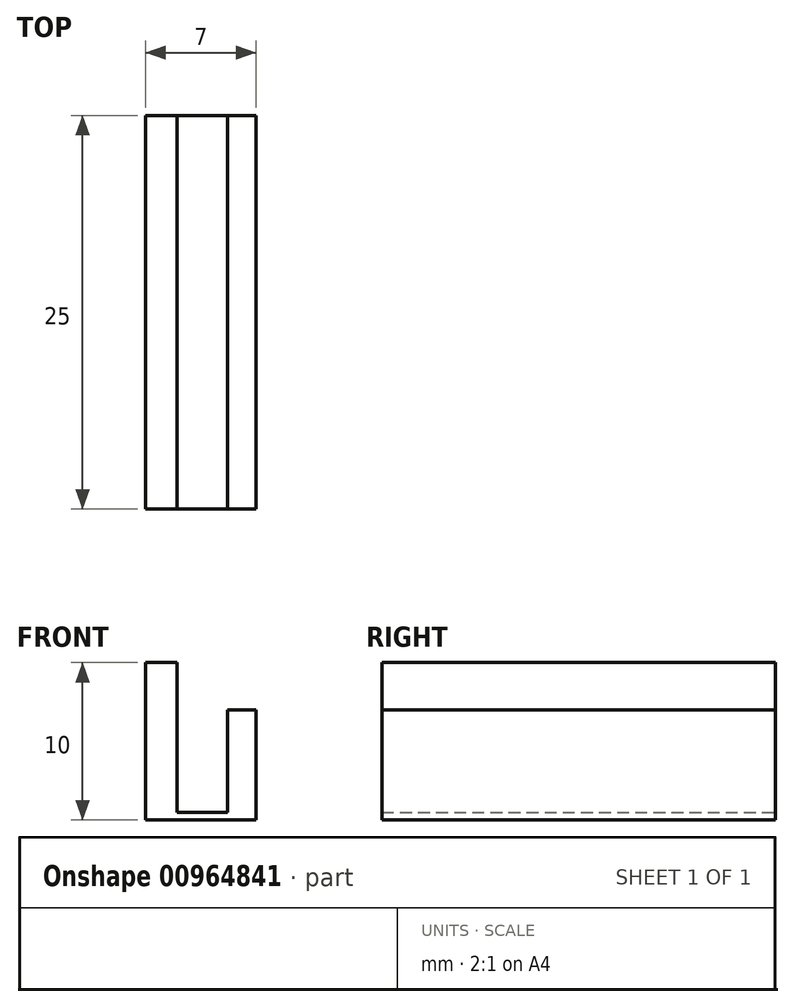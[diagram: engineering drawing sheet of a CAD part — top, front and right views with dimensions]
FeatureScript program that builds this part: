
annotation { "Feature Type Name" : "Feature", "Feature Type Description" : "" }
export const myFeature = defineFeature(function(context is Context, id is Id, definition is map)
    precondition{}
    {
        {
            var Q0;
            Q0=qCreatedBy(makeId("Front.planeOp"),FACE);
            var sketch = newSketch(context, id + "F0", { "sketchPlane" : qUnion([Q0])});
            skLineSegment(sketch, "E0", {"start": v(0, 0) * mm, "end": v(7, 0) * mm});
            skLineSegment(sketch, "E1", {"start": v(0, 0) * mm, "end": v(0, 2) * mm});
            skLineSegment(sketch, "E2", {"start": v(0, 2) * mm, "end": v(0, 10) * mm});
            skLineSegment(sketch, "E3", {"start": v(0, 10) * mm, "end": v(2, 10) * mm});
            skLineSegment(sketch, "E4", {"start": v(2, 10) * mm, "end": v(2, 0.5) * mm});
            skLineSegment(sketch, "E5", {"start": v(2, 0.5) * mm, "end": v(5.2, 0.5) * mm});
            skLineSegment(sketch, "E6", {"start": v(7, 0) * mm, "end": v(7, 7) * mm});
            skLineSegment(sketch, "E7", {"start": v(7, 7) * mm, "end": v(5.2, 7) * mm});
            skLineSegment(sketch, "E8", {"start": v(5.2, 7) * mm, "end": v(5.2, 0.5) * mm});
            skSolve(sketch);
        }
        {
            var Q0;
            Q0=makeQuery(id+"F0.imprint","IMPRINT",FACE,{"disambiguationData":[TD([[makeQuery(id+"F0.imprint","IMPRINT",EDGE,{"derivedFrom":sQuery(id+"F0.wireOp",EDGE,"E0")}),1.0]])]});
            extrude(context, id + "F1", {"entities" : qUnion([Q0]), "depth" : 25 * mm, "offsetDistance" : 25 * mm});
        }
    });
